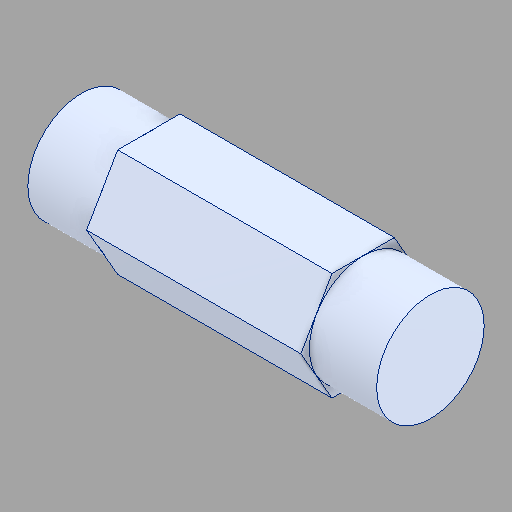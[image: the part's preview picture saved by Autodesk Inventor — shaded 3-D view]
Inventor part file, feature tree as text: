
AUTODESK INVENTOR PART (.ipt)
format: ipt  version: 2024.2 (Build 282272000, 272)  size: 103,936 bytes
history: native  units: in
note: dims shown in document units (in); Inventor stores cm internally (conversion verified against a paired STEP export)
features: mirror x1
ambient origin geometry x8: Origin, YZ Plane, XZ Plane, XY Plane, X Axis, Y Axis, Z Axis, Center Point
bodies: Solid1 (feature_tree)
feature tree (1):
  mirror  "Mirror1"
